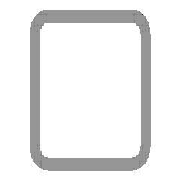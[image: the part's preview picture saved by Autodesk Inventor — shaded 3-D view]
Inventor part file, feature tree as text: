
AUTODESK INVENTOR PART (.ipt)
format: ipt  version: 2022 (Build 260153000, 153)  size: 264,704 bytes
history: native  units: mm (DEFAULTED — no unit token found)
features: other x7, sketch x3, surface_op x2, plane x1
ambient origin geometry x8: Origin, YZ Plane, XZ Plane, XY Plane, X Axis, Y Axis, Z Axis, Center Point
bodies: Body (feature_tree), Solid7 (feature_tree)
feature tree (13):
  parser-record x1  (decoder bookkeeping rows leaked as tree rows — omitted from the tree; the rows remain in map.json)
  other  "Driven Length"
  other  "Start Plane"
  other  "End Plane"
  sketch  "Sketch"  dims[d7=8.0mm d9=40.0mm d11=40.0mm d12=4.0mm d13=-0.0mm d14=180.0mm d15=20.0mm d16=20.0mm d17=90.0deg d18=180.0mm d109=5.0mm d110=5.0mm d111=5.0mm d112=5.0mm d113=5.0mm d114=5.0mm d115=5.0mm d116=5.0mm d117=0.0mm d118=5.0mm d119=5.0mm d120=5.0mm d121=5.0mm d122=5.0mm d123=5.0mm d124=5.0mm d125=5.0mm d126=0.0mm]
  sketch  "Sketch3"  dims[d3=155.0mm]
  plane  "Work Plane3"
  sketch  "Sketch4"  dims[d4=0.0mm]
  other  "Srf17"
  other  "Srf18"
  other  "Srf16"
  surface_op  "Boundary Patch11"
  surface_op  "Boundary Patch12"
